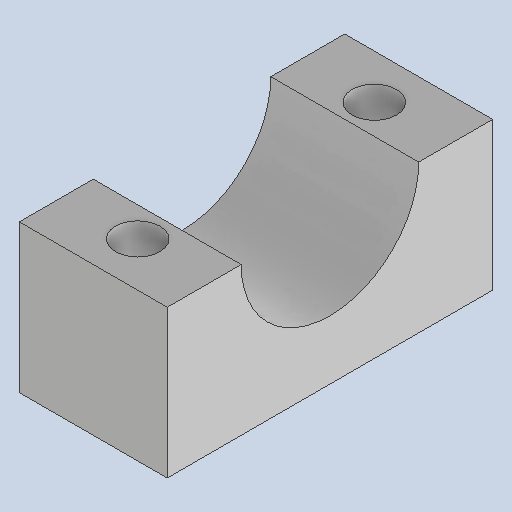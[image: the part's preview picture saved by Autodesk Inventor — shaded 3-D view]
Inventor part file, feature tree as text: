
AUTODESK INVENTOR PART (.ipt)
format: ipt  version: 2025.1 (Build 291241000, 241)  size: 110,080 bytes
history: native  units: mm
features: other x3, sketch x2
ambient origin geometry x8: Origin, YZ Plane, XZ Plane, XY Plane, X Axis, Y Axis, Z Axis, Center Point
bodies: Solid1 (feature_tree)
feature tree (5):
  other  "145 part.ipt"
  other  "Solid1::145 part.ipt"
  other  "Bezeichnung1"
  sketch  "Sketch1"  dims[d0=10.0mm]
  sketch  "Sketch2"
